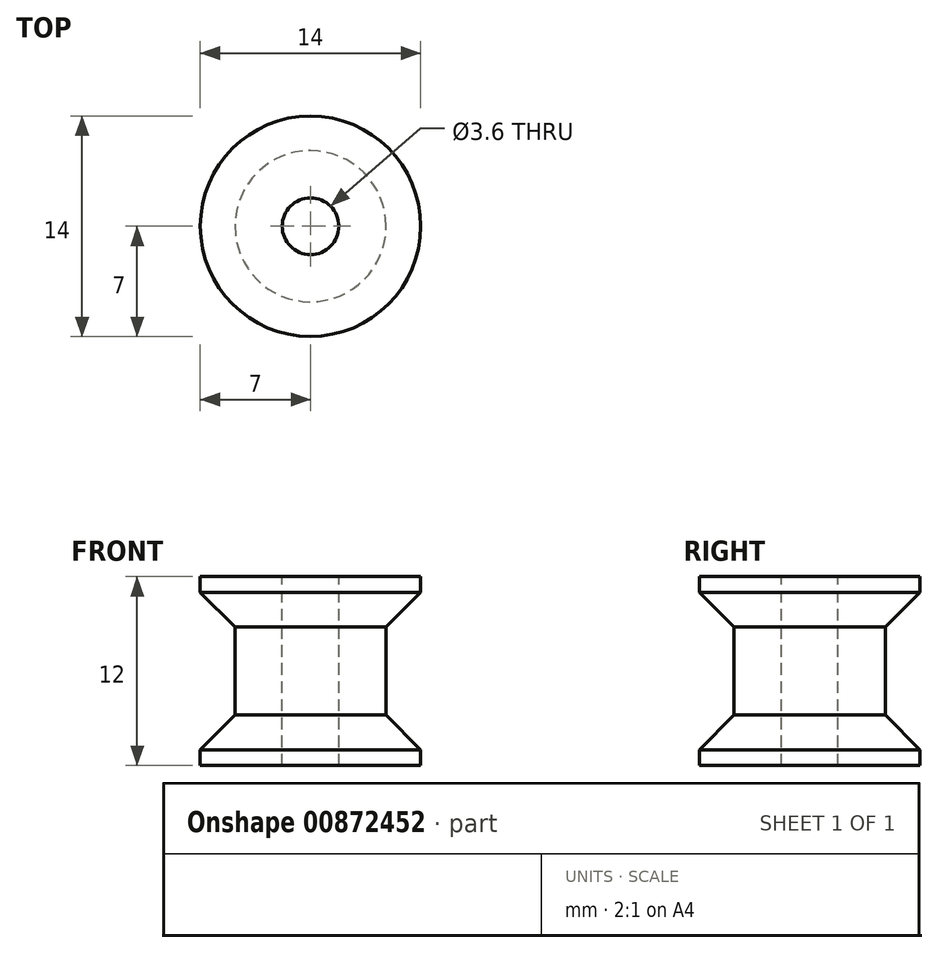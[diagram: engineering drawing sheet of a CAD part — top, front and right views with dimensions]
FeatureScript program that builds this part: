
annotation { "Feature Type Name" : "Feature", "Feature Type Description" : "" }
export const myFeature = defineFeature(function(context is Context, id is Id, definition is map)
    precondition{}
    {
        {
            var Q0;
            Q0=qCreatedBy(makeId("Front.planeOp"),FACE);
            var sketch = newSketch(context, id + "F0", { "sketchPlane" : qUnion([Q0])});
            skLineSegment(sketch, "E0", {"start": v(0, 12.72) * mm, "end": v(0, -14.25) * mm, "construction": true});
            skLineSegment(sketch, "E1.bottom", {"start": v(-4.8, 6) * mm, "end": v(-1.8, 6) * mm});
            skLineSegment(sketch, "E1.top", {"start": v(-4.8, 0) * mm, "end": v(-1.8, 0) * mm});
            skLineSegment(sketch, "E1.right", {"start": v(-1.8, 6) * mm, "end": v(-1.8, 0) * mm});
            skLineSegment(sketch, "E2", {"start": v(-27.3, 0) * mm, "end": v(-24.3, 0) * mm, "construction": true});
            skLineSegment(sketch, "E3.bottom", {"start": v(-4.8, 6) * mm, "end": v(-7, 6) * mm});
            skLineSegment(sketch, "E4", {"start": v(-7, 6) * mm, "end": v(-7, 5) * mm});
            skLineSegment(sketch, "E5", {"start": v(-4.8, 6) * mm, "end": v(-4.8, 2.8) * mm});
            skLineSegment(sketch, "E6", {"start": v(-4.8, 2.8) * mm, "end": v(-4.8, 0) * mm});
            skLineSegment(sketch, "E7", {"start": v(-4.8, 2.8) * mm, "end": v(-7, 5) * mm});
            skLineSegment(sketch, "E8.MirrorCS", {"start": v(-4.8, -2.8) * mm, "end": v(-7, -5) * mm});
            skLineSegment(sketch, "E9.MirrorCS", {"start": v(-4.8, -6) * mm, "end": v(-7, -6) * mm});
            skLineSegment(sketch, "E10.MirrorCS", {"start": v(-4.8, -6) * mm, "end": v(-1.8, -6) * mm});
            skLineSegment(sketch, "E11.MirrorCS", {"start": v(-1.8, -6) * mm, "end": v(-1.8, 0) * mm});
            skLineSegment(sketch, "E12.MirrorCS", {"start": v(-7, -6) * mm, "end": v(-7, -5) * mm});
            skLineSegment(sketch, "E13.MirrorCS", {"start": v(-4.8, -6) * mm, "end": v(-4.8, -2.8) * mm});
            skLineSegment(sketch, "E14.MirrorCS", {"start": v(-4.8, -2.8) * mm, "end": v(-4.8, 0) * mm});
            skSolve(sketch);
        }
        {
            var Q0;
            Q0=makeQuery(id+"F0.imprint","IMPRINT",FACE,{"disambiguationData":[TD([[makeQuery(id+"F0.imprint","IMPRINT",EDGE,{"derivedFrom":sQuery(id+"F0.wireOp",EDGE,"E10.MirrorCS")}),1.0]])]});
            var Q1;
            Q1=makeQuery(id+"F0.imprint","IMPRINT",FACE,{"disambiguationData":[TD([[makeQuery(id+"F0.imprint","IMPRINT",EDGE,{"derivedFrom":sQuery(id+"F0.wireOp",EDGE,"E3.bottom")}),1.0]])]});
            var Q2;
            Q2=makeQuery(id+"F0.imprint","IMPRINT",FACE,{"disambiguationData":[TD([[makeQuery(id+"F0.imprint","IMPRINT",EDGE,{"derivedFrom":sQuery(id+"F0.wireOp",EDGE,"E1.bottom")}),-1.0]])]});
            var Q3;
            Q3=makeQuery(id+"F0.imprint","IMPRINT",FACE,{"disambiguationData":[TD([[makeQuery(id+"F0.imprint","IMPRINT",EDGE,{"derivedFrom":sQuery(id+"F0.wireOp",EDGE,"E8.MirrorCS")}),1.0]])]});
            var Q4;
            Q4=sQuery(id+"F0.wireOp",EDGE,"E0");
            revolve(context, id + "F1", {"surfaceOperationType" : NewSurfaceOperationType.NEW, "entities" : qUnion([Q0, Q1, Q2, Q3]), "axis" : qUnion([Q4]), "revolveType" : RevolveType.FULL});
        }
    });
